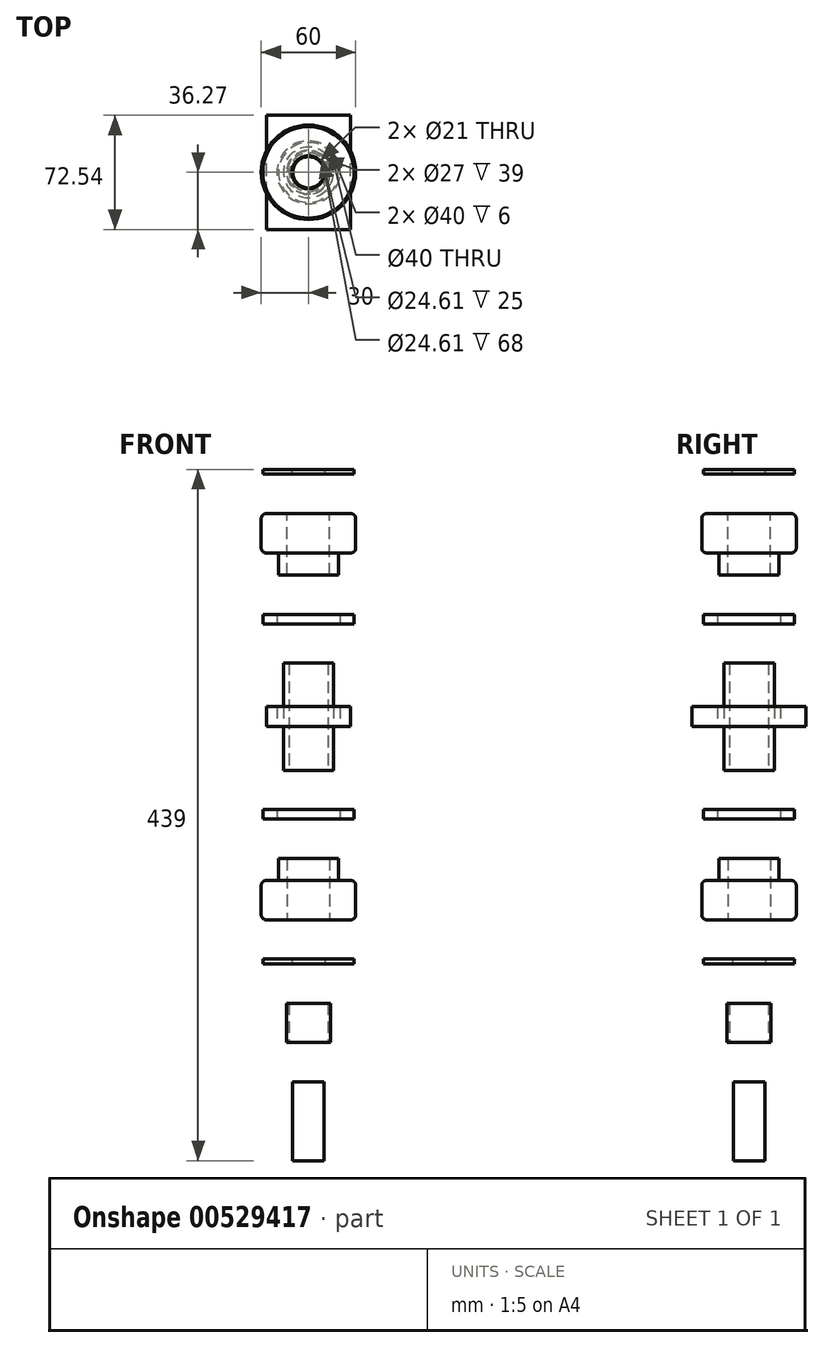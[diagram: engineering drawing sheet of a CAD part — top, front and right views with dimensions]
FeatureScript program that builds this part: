
annotation { "Feature Type Name" : "Feature", "Feature Type Description" : "" }
export const myFeature = defineFeature(function(context is Context, id is Id, definition is map)
    precondition{}
    {
        {
            var Q0;
            Q0=qCreatedBy(makeId("Top.planeOp"),FACE);
            var sketch = newSketch(context, id + "F0", { "sketchPlane" : qUnion([Q0])});
            skCircle(sketch, "E0", {"center": v(0, 0) * mm, "radius": 10 * mm});
            skSolve(sketch);
        }
        {
            var Q0;
            Q0 = qSketchRegion(id + "F0", true);
            extrude(context, id + "F1", {"entities" : qUnion([Q0]), "depth" : 50 * mm, "offsetDistance" : 25 * mm});
        }
        {
            var Q0;
            Q0=makeQuery(id+"F1.opExtrude","CAP_FACE",FACE,{"disambiguationData":[OSD([sQuery(id+"F0.wireOp",EDGE,"E0")])],"isStart":false});
            cPlane(context, id + "F2", {"entities" : qUnion([Q0]), "cplaneType" : CPlaneType.OFFSET, "offset" : 25 * mm, "width" : 150 * mm, "height" : 150 * mm});
        }
        {
            var Q0;
            Q0=qCreatedBy(id+"F2.planeOp",FACE);
            var sketch = newSketch(context, id + "F3", { "sketchPlane" : qUnion([Q0])});
            skCircle(sketch, "E1", {"center": v(0, 0) * mm, "radius": 12.3 * mm});
            skCircle(sketch, "E2", {"center": v(0, 0) * mm, "radius": 14 * mm});
            skSolve(sketch);
        }
        {
            var Q0;
            Q0=makeQuery(id+"F3.imprint","IMPRINT",FACE,{"disambiguationData":[TD([[makeQuery(id+"F3.imprint","IMPRINT",EDGE,{"derivedFrom":sQuery(id+"F3.wireOp",EDGE,"E1")}),-1.0]])]});
            extrude(context, id + "F4", {"entities" : qUnion([Q0]), "depth" : 25 * mm, "offsetDistance" : 25 * mm});
        }
        {
            var Q0;
            Q0=makeQuery(id+"F4.opExtrude","CAP_FACE",FACE,{"disambiguationData":[OSD([sQuery(id+"F3.wireOp",EDGE,"E1"),sQuery(id+"F3.wireOp",EDGE,"E2")])],"isStart":false});
            cPlane(context, id + "F5", {"entities" : qUnion([Q0]), "cplaneType" : CPlaneType.OFFSET, "offset" : 25 * mm, "width" : 150 * mm, "height" : 150 * mm});
        }
        {
            var Q0;
            Q0=qCreatedBy(id+"F5.planeOp",FACE);
            var sketch = newSketch(context, id + "F6", { "sketchPlane" : qUnion([Q0])});
            skCircle(sketch, "E3", {"center": v(0, 0) * mm, "radius": 10.5 * mm});
            skCircle(sketch, "E4", {"center": v(0, 0) * mm, "radius": 29 * mm});
            skSolve(sketch);
        }
        {
            var Q0;
            Q0=makeQuery(id+"F6.imprint","IMPRINT",FACE,{"disambiguationData":[TD([[makeQuery(id+"F6.imprint","IMPRINT",EDGE,{"derivedFrom":sQuery(id+"F6.wireOp",EDGE,"E3")}),-1.0]])]});
            extrude(context, id + "F7", {"entities" : qUnion([Q0]), "depth" : 3 * mm, "offsetDistance" : 25 * mm});
        }
        {
            var Q0;
            Q0=makeQuery(id+"F7.opExtrude","CAP_FACE",FACE,{"disambiguationData":[OSD([sQuery(id+"F6.wireOp",EDGE,"E3"),sQuery(id+"F6.wireOp",EDGE,"E4")])],"isStart":false});
            cPlane(context, id + "F8", {"entities" : qUnion([Q0]), "cplaneType" : CPlaneType.OFFSET, "offset" : 25 * mm, "width" : 150 * mm, "height" : 150 * mm});
        }
        {
            var Q0;
            Q0=qCreatedBy(id+"F8.planeOp",FACE);
            var sketch = newSketch(context, id + "F9", { "sketchPlane" : qUnion([Q0])});
            skCircle(sketch, "E5", {"center": v(0, 0) * mm, "radius": 13.5 * mm});
            skCircle(sketch, "E6", {"center": v(0, 0) * mm, "radius": 30 * mm});
            skSolve(sketch);
        }
        {
            var Q0;
            Q0=makeQuery(id+"F9.imprint","IMPRINT",FACE,{"disambiguationData":[TD([[makeQuery(id+"F9.imprint","IMPRINT",EDGE,{"derivedFrom":sQuery(id+"F9.wireOp",EDGE,"E5")}),-1.0]])]});
            extrude(context, id + "F10", {"entities" : qUnion([Q0]), "depth" : 25 * mm, "offsetDistance" : 25 * mm});
        }
        {
            var Q0;
            Q0=makeQuery(id+"F10.opExtrude","CAP_FACE",FACE,{"disambiguationData":[OSD([sQuery(id+"F9.wireOp",EDGE,"E5"),sQuery(id+"F9.wireOp",EDGE,"E6")])],"isStart":false});
            var sketch = newSketch(context, id + "F11", { "sketchPlane" : qUnion([Q0])});
            skCircle(sketch, "E7", {"center": v(0, 0) * mm, "radius": 19 * mm});
            skCircle(sketch, "E8", {"center": v(0, 0) * mm, "radius": 13.5 * mm});
            skSolve(sketch);
        }
        {
            var Q0;
            Q0=makeQuery(id+"F11.imprint","IMPRINT",FACE,{"disambiguationData":[TD([[makeQuery(id+"F11.imprint","IMPRINT",EDGE,{"derivedFrom":sQuery(id+"F11.wireOp",EDGE,"E7")}),1.0]])]});
            extrude(context, id + "F12", {"entities" : qUnion([Q0]), "operationType" : NewBodyOperationType.ADD, "depth" : 14 * mm, "offsetDistance" : 25 * mm});
        }
        {
            var Q0;
            Q0=makeQuery(id+"F12.opExtrude","CAP_FACE",FACE,{"disambiguationData":[OSD([sQuery(id+"F11.wireOp",EDGE,"E7"),sQuery(id+"F11.wireOp",EDGE,"E8")])],"isStart":false});
            cPlane(context, id + "F13", {"entities" : qUnion([Q0]), "cplaneType" : CPlaneType.OFFSET, "offset" : 25 * mm, "width" : 150 * mm, "height" : 150 * mm});
        }
        {
            var Q0;
            Q0=qCreatedBy(id+"F13.planeOp",FACE);
            var sketch = newSketch(context, id + "F14", { "sketchPlane" : qUnion([Q0])});
            skCircle(sketch, "E9", {"center": v(0, 0) * mm, "radius": 20 * mm});
            skCircle(sketch, "E10", {"center": v(0, 0) * mm, "radius": 29 * mm});
            skSolve(sketch);
        }
        {
            var Q0;
            Q0=makeQuery(id+"F14.imprint","IMPRINT",FACE,{"disambiguationData":[TD([[makeQuery(id+"F14.imprint","IMPRINT",EDGE,{"derivedFrom":sQuery(id+"F14.wireOp",EDGE,"E9")}),-1.0]])]});
            extrude(context, id + "F15", {"entities" : qUnion([Q0]), "depth" : 6 * mm, "offsetDistance" : 25 * mm});
        }
        {
            var Q0;
            Q0=makeQuery(id+"F15.opExtrude","CAP_FACE",FACE,{"disambiguationData":[OSD([sQuery(id+"F14.wireOp",EDGE,"E9"),sQuery(id+"F14.wireOp",EDGE,"E10")])],"isStart":false});
            cPlane(context, id + "F16", {"entities" : qUnion([Q0]), "cplaneType" : CPlaneType.OFFSET, "offset" : 25 * mm, "width" : 150 * mm, "height" : 150 * mm});
        }
        {
            var Q0;
            Q0=qCreatedBy(id+"F16.planeOp",FACE);
            var sketch = newSketch(context, id + "F17", { "sketchPlane" : qUnion([Q0])});
            skCircle(sketch, "E11", {"center": v(0, 0) * mm, "radius": 12.3 * mm});
            skCircle(sketch, "E12", {"center": v(0, 0) * mm, "radius": 16 * mm});
            skSolve(sketch);
        }
        {
            var Q0;
            Q0=makeQuery(id+"F17.imprint","IMPRINT",FACE,{"disambiguationData":[TD([[makeQuery(id+"F17.imprint","IMPRINT",EDGE,{"derivedFrom":sQuery(id+"F17.wireOp",EDGE,"E11")}),-1.0]])]});
            extrude(context, id + "F18", {"entities" : qUnion([Q0]), "depth" : 68 * mm, "offsetDistance" : 25 * mm});
        }
        {
            var Q0;
            Q0=makeQuery(id+"F18.opExtrude","CAP_FACE",FACE,{"disambiguationData":[OSD([sQuery(id+"F17.wireOp",EDGE,"E11"),sQuery(id+"F17.wireOp",EDGE,"E12")])],"isStart":false});
            cPlane(context, id + "F19", {"entities" : qUnion([Q0]), "cplaneType" : CPlaneType.OFFSET, "offset" : 25 * mm, "width" : 150 * mm, "height" : 150 * mm});
        }
        {
            var Q0;
            Q0=makeQuery(id+"F15.opExtrude","SWEPT_BODY",BODY,{"disambiguationData":[OSD([sQuery(id+"F14.wireOp",EDGE,"E9"),sQuery(id+"F14.wireOp",EDGE,"E10")])]});
            var Q1;
            Q1=qCreatedBy(id+"F19.planeOp",FACE);
            transform(context, id + "F20", {"entities" : qUnion([Q0]), "transformType" : TransformType.TRANSLATION_DISTANCE, "transformDirection" : qUnion([Q1]), "distance" : (25 + 68 + 25 + 6) * mm, "makeCopy" : true});
        }
        {
            var Q0;
            Q0=qCreatedBy(id+"F16.planeOp",FACE);
            cPlane(context, id + "F21", {"entities" : qUnion([Q0]), "cplaneType" : CPlaneType.OFFSET, "offset" : 34 * mm, "width" : 150 * mm, "height" : 150 * mm});
        }
        {
            var Q0;
            Q0=makeQuery(id+"F10.opExtrude","CAP_EDGE",EDGE,{"disambiguationData":[OSD([sQuery(id+"F9.wireOp",EDGE,"E6")])],"isStart":false});
            var Q1;
            Q1=makeQuery(id+"F10.opExtrude","CAP_EDGE",EDGE,{"disambiguationData":[OSD([sQuery(id+"F9.wireOp",EDGE,"E6")])],"isStart":true});
            fillet(context, id + "F22", {"entities" : qUnion([Q0, Q1]), "radius" : 3.17 * mm, "tangentPropagation" : true, "allowEdgeOverflow" : false});
        }
        {
            var Q0;
            Q0=makeQuery(id+"F10.opExtrude","SWEPT_BODY",BODY,{"disambiguationData":[OSD([sQuery(id+"F9.wireOp",EDGE,"E5"),sQuery(id+"F9.wireOp",EDGE,"E6")])]});
            var Q1;
            Q1=makeQuery(id+"F7.opExtrude","SWEPT_BODY",BODY,{"disambiguationData":[OSD([sQuery(id+"F6.wireOp",EDGE,"E3"),sQuery(id+"F6.wireOp",EDGE,"E4")])]});
            var Q2;
            Q2=qCreatedBy(id+"F21.planeOp",FACE);
            mirror(context, id + "F23", {"entities" : qUnion([Q0, Q1]), "mirrorPlane" : qUnion([Q2])});
        }
        {
            var Q0;
            Q0=qCreatedBy(id+"F21.planeOp",FACE);
            var sketch = newSketch(context, id + "F24", { "sketchPlane" : qUnion([Q0])});
            skCircle(sketch, "E13", {"center": v(0, 0) * mm, "radius": 20 * mm});
            skLineSegment(sketch, "E14.bottom", {"start": v(-26.66, -36.27) * mm, "end": v(26.66, -36.27) * mm});
            skLineSegment(sketch, "E14.top", {"start": v(-26.66, 36.27) * mm, "end": v(26.66, 36.27) * mm});
            skLineSegment(sketch, "E14.left", {"start": v(-26.66, -36.27) * mm, "end": v(-26.66, 36.27) * mm});
            skLineSegment(sketch, "E14.right", {"start": v(26.66, -36.27) * mm, "end": v(26.66, 36.27) * mm});
            skSolve(sketch);
        }
        {
            var Q0;
            Q0=makeQuery(id+"F24.imprint","IMPRINT",FACE,{"disambiguationData":[TD([[makeQuery(id+"F24.imprint","IMPRINT",EDGE,{"derivedFrom":sQuery(id+"F24.wireOp",EDGE,"E13")}),-1.0]])]});
            extrude(context, id + "F25", {"entities" : qUnion([Q0]), "endBound" : BoundingType.SYMMETRIC, "depth" : 12.7 * mm, "offsetDistance" : 25 * mm});
        }
    });
